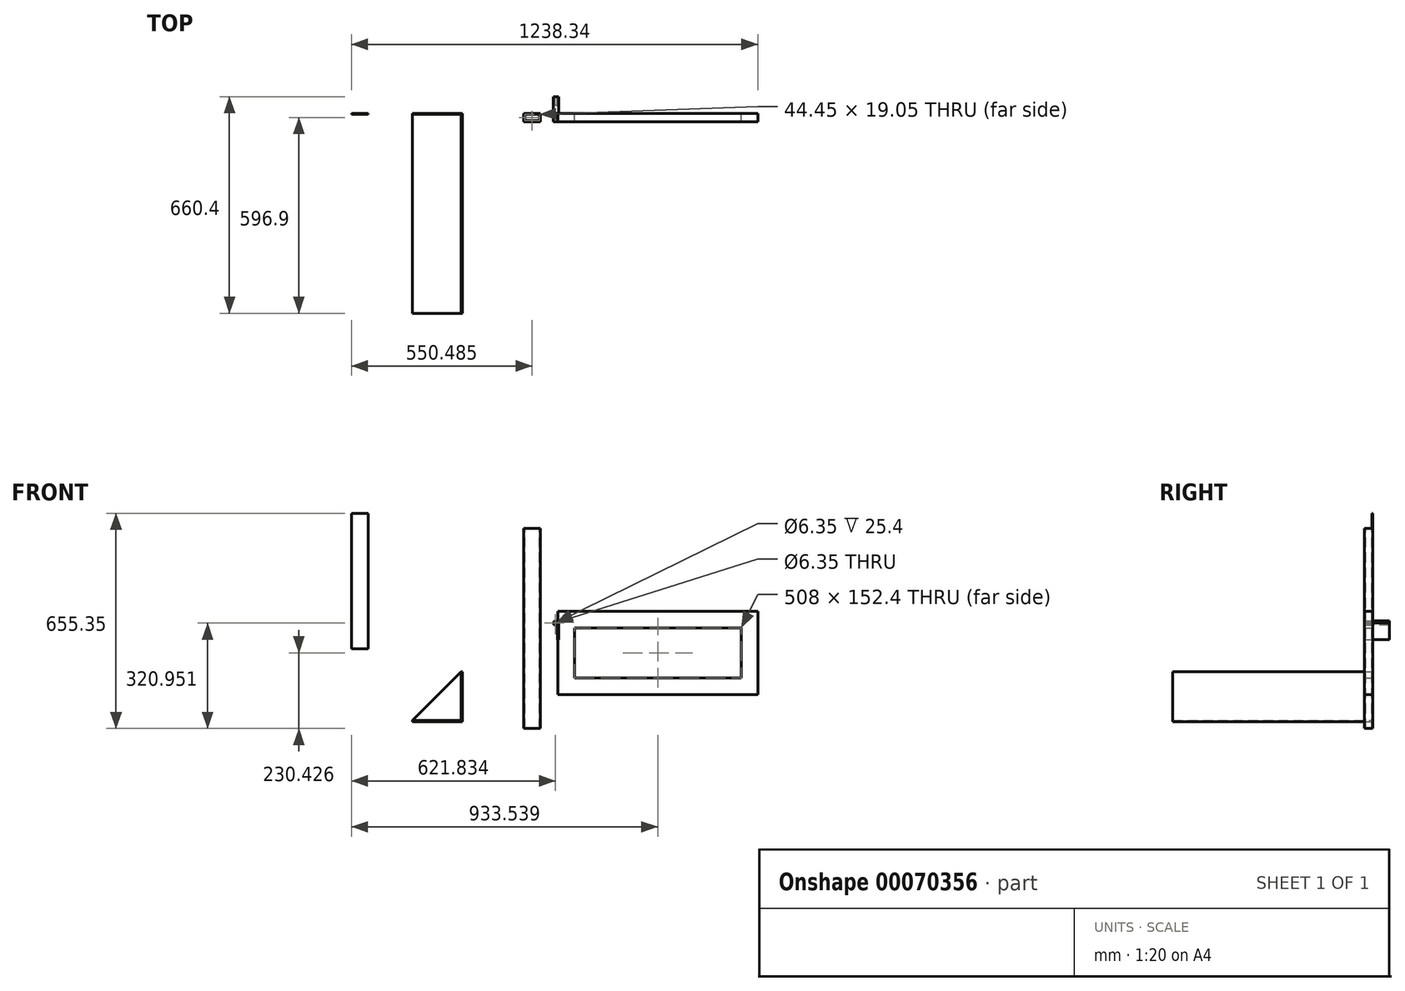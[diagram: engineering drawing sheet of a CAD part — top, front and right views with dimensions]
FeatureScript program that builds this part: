
annotation { "Feature Type Name" : "Feature", "Feature Type Description" : "" }
export const myFeature = defineFeature(function(context is Context, id is Id, definition is map)
    precondition{}
    {
        {
            var Q0;
            Q0=qCreatedBy(makeId("Front.planeOp"),FACE);
            var sketch = newSketch(context, id + "F0", { "sketchPlane" : qUnion([Q0])});
            skLineSegment(sketch, "E0.bottom", {"start": v(-403.8, -283.31) * mm, "end": v(-251.4, -283.31) * mm});
            skLineSegment(sketch, "E0.top", {"start": v(-403.8, -286.49) * mm, "end": v(-251.4, -286.49) * mm});
            skLineSegment(sketch, "E0.left", {"start": v(-403.8, -283.31) * mm, "end": v(-403.8, -286.49) * mm});
            skLineSegment(sketch, "E0.right", {"start": v(-251.4, -283.31) * mm, "end": v(-251.4, -286.49) * mm});
            skLineSegment(sketch, "E1.bottom", {"start": v(-251.4, -286.49) * mm, "end": v(-254.57, -286.49) * mm});
            skLineSegment(sketch, "E1.top", {"start": v(-251.4, -134.09) * mm, "end": v(-254.57, -134.09) * mm});
            skLineSegment(sketch, "E1.left", {"start": v(-251.4, -286.49) * mm, "end": v(-251.4, -134.09) * mm});
            skLineSegment(sketch, "E1.right", {"start": v(-254.57, -286.49) * mm, "end": v(-254.57, -134.09) * mm});
            skLineSegment(sketch, "E2", {"start": v(-254.57, -134.09) * mm, "end": v(-403.8, -283.31) * mm});
            skSolve(sketch);
        }
        {
            var Q0;
            {var subQ4=sQuery(id+"F0.wireOp",EDGE,"E0.top");Q0=makeQuery(id+"F0.imprint","IMPRINT",FACE,{"disambiguationData":[TD([[makeQuery(id+"F0.imprint","IMPRINT",EDGE,{"derivedFrom":subQ4}),1.0]])]});}
            var Q1;
            {var subQ5=sQuery(id+"F0.wireOp",EDGE,"E1.bottom");Q1=makeQuery(id+"F0.imprint","IMPRINT",FACE,{"disambiguationData":[TD([[makeQuery(id+"F0.imprint","IMPRINT",EDGE,{"derivedFrom":subQ5}),-1.0]])]});}
            var Q2;
            {var subQ5=sQuery(id+"F0.wireOp",EDGE,"E1.top");Q2=makeQuery(id+"F0.imprint","IMPRINT",FACE,{"disambiguationData":[TD([[makeQuery(id+"F0.imprint","IMPRINT",EDGE,{"derivedFrom":subQ5}),1.0]])]});}
            extrude(context, id + "F1", {"entities" : qUnion([Q0, Q1, Q2]), "depth" : 609.6 * mm});
        }
        {
            var Q0;
            {var subQ0=sQuery(id+"F0.wireOp",EDGE,"E2");Q0=makeQuery(id+"F0.imprint","IMPRINT",FACE,{"disambiguationData":[TD([[makeQuery(id+"F0.imprint","IMPRINT",EDGE,{"derivedFrom":subQ0}),1.0]])]});}
            extrude(context, id + "F2", {"entities" : qUnion([Q0]), "depth" : 3.17 * mm});
        }
        {
            var Q0;
            Q0=qCreatedBy(makeId("Front.planeOp"),FACE);
            var sketch = newSketch(context, id + "F3", { "sketchPlane" : qUnion([Q0])});
            skCircle(sketch, "E3", {"center": v(32.81, 13.43) * mm, "radius": 6.35 * mm});
            skLineSegment(sketch, "E4.bottom", {"start": v(39.16, 13.43) * mm, "end": v(42.34, 13.43) * mm});
            skLineSegment(sketch, "E4.top", {"start": v(39.16, -37.37) * mm, "end": v(42.34, -37.37) * mm});
            skLineSegment(sketch, "E4.left", {"start": v(39.16, 13.43) * mm, "end": v(39.16, -37.37) * mm});
            skLineSegment(sketch, "E4.right", {"start": v(42.34, 13.43) * mm, "end": v(42.34, -37.37) * mm});
            skCircle(sketch, "E5", {"center": v(32.81, 13.43) * mm, "radius": 3.18 * mm});
            skLineSegment(sketch, "E6", {"start": v(42.34, 13.43) * mm, "end": v(37.05, 18.16) * mm});
            skLineSegment(sketch, "E7", {"start": v(32.81, 7.08) * mm, "end": v(39.16, 7.08) * mm});
            skSolve(sketch);
        }
        {
            var Q0;
            Q0=makeQuery(id+"F3.imprint","IMPRINT",FACE,{"disambiguationData":[TD([[makeQuery(id+"F3.imprint","IMPRINT",EDGE,{"derivedFrom":sQuery(id+"F3.wireOp",EDGE,"E5")}),-1.0]])]});
            var Q1;
            {var subQ0=sQuery(id+"F3.wireOp",EDGE,"E4.bottom");Q1=makeQuery(id+"F3.imprint","IMPRINT",FACE,{"disambiguationData":[TD([[makeQuery(id+"F3.imprint","IMPRINT",EDGE,{"derivedFrom":subQ0}),1.0]])]});}
            var Q2;
            {var subQ3=sQuery(id+"F3.wireOp",EDGE,"E7");Q2=makeQuery(id+"F3.imprint","IMPRINT",FACE,{"disambiguationData":[TD([[makeQuery(id+"F3.imprint","IMPRINT",EDGE,{"derivedFrom":subQ3}),1.0]])]});}
            var Q3;
            {var subQ1=sQuery(id+"F3.wireOp",EDGE,"E4.bottom");Q3=makeQuery(id+"F3.imprint","IMPRINT",FACE,{"disambiguationData":[TD([[makeQuery(id+"F3.imprint","IMPRINT",EDGE,{"derivedFrom":subQ1}),-1.0]])]});}
            extrude(context, id + "F4", {"entities" : qUnion([Q0, Q1, Q2, Q3]), "depth" : 25.4 * mm});
        }
        {
            var Q0;
            {var subQ1=sQuery(id+"F3.wireOp",EDGE,"E4.bottom");Q0=makeQuery(id+"F3.imprint","IMPRINT",FACE,{"disambiguationData":[TD([[makeQuery(id+"F3.imprint","IMPRINT",EDGE,{"derivedFrom":subQ1}),-1.0]])]});}
            var Q1;
            {var subQ3=sQuery(id+"F3.wireOp",EDGE,"E7");Q1=makeQuery(id+"F3.imprint","IMPRINT",FACE,{"disambiguationData":[TD([[makeQuery(id+"F3.imprint","IMPRINT",EDGE,{"derivedFrom":subQ3}),1.0]])]});}
            var Q2;
            {var subQ0=sQuery(id+"F3.wireOp",EDGE,"E4.bottom");Q2=makeQuery(id+"F3.imprint","IMPRINT",FACE,{"disambiguationData":[TD([[makeQuery(id+"F3.imprint","IMPRINT",EDGE,{"derivedFrom":subQ0}),1.0]])]});}
            var Q3;
            Q3=makeQuery(id+"F3.imprint","IMPRINT",FACE,{"disambiguationData":[TD([[makeQuery(id+"F3.imprint","IMPRINT",EDGE,{"derivedFrom":sQuery(id+"F3.wireOp",EDGE,"E5")}),-1.0]])]});
            var Q4;
            Q4=makeQuery(id+"F3.imprint","IMPRINT",FACE,{"disambiguationData":[TD([[makeQuery(id+"F3.imprint","IMPRINT",EDGE,{"derivedFrom":sQuery(id+"F3.wireOp",EDGE,"E5")}),1.0]])]});
            extrude(context, id + "F5", {"entities" : qUnion([Q0, Q1, Q2, Q3, Q4]), "oppositeDirection" : true, "depth" : 25.4 * mm});
        }
        {
            var Q0;
            Q0=makeQuery(id+"F5.opExtrude","CAP_FACE",FACE,{"disambiguationData":[OSD([sQuery(id+"F3.wireOp",EDGE,"E3"),sQuery(id+"F3.wireOp",EDGE,"E4.top"),sQuery(id+"F3.wireOp",EDGE,"E4.left"),sQuery(id+"F3.wireOp",EDGE,"E4.right"),sQuery(id+"F3.wireOp",EDGE,"E6"),sQuery(id+"F3.wireOp",EDGE,"E7")])],"isStart":false});
            var sketch = newSketch(context, id + "F6", { "sketchPlane" : qUnion([Q0])});
            skCircle(sketch, "E8.0", {"center": v(-32.81, 13.43) * mm, "radius": 3.18 * mm});
            skSolve(sketch);
        }
        {
            var Q0;
            Q0=makeQuery(id+"F6.imprint","IMPRINT",FACE,{"disambiguationData":[TD([[makeQuery(id+"F6.imprint","IMPRINT",EDGE,{"derivedFrom":sQuery(id+"F6.wireOp",EDGE,"E8.0")}),-1.0]])]});
            extrude(context, id + "F7", {"entities" : qUnion([Q0]), "operationType" : NewBodyOperationType.ADD, "depth" : 25.4 * mm});
        }
        {
            var Q0;
            Q0=qCreatedBy(makeId("Front.planeOp"),FACE);
            var sketch = newSketch(context, id + "F8", { "sketchPlane" : qUnion([Q0])});
            skLineSegment(sketch, "E9.bottom", {"start": v(-13.13, 302.08) * mm, "end": v(-63.93, 302.08) * mm});
            skLineSegment(sketch, "E9.top", {"start": v(-13.13, -307.52) * mm, "end": v(-63.93, -307.52) * mm});
            skLineSegment(sketch, "E9.left", {"start": v(-13.13, 302.08) * mm, "end": v(-13.13, -307.52) * mm});
            skLineSegment(sketch, "E9.right", {"start": v(-63.93, 302.08) * mm, "end": v(-63.93, -307.52) * mm});
            skSolve(sketch);
        }
        {
            var Q0;
            Q0 = qSketchRegion(id + "F8", true);
            extrude(context, id + "F9", {"entities" : qUnion([Q0]), "depth" : 25.4 * mm});
        }
        {
            var Q0;
            Q0=makeQuery(id+"F9.opExtrude","SWEPT_FACE",FACE,{"disambiguationData":[OSD([sQuery(id+"F8.wireOp",EDGE,"E9.bottom")])]});
            var sketch = newSketch(context, id + "F10", { "sketchPlane" : qUnion([Q0])});
            skLineSegment(sketch, "E10.0", {"start": v(-13.13, -25.4) * mm, "end": v(-63.93, -25.4) * mm});
            skLineSegment(sketch, "E10.1", {"start": v(-13.13, -25.4) * mm, "end": v(-13.13, 0) * mm});
            skLineSegment(sketch, "E10.2", {"start": v(-13.13, 0) * mm, "end": v(-63.93, 0) * mm});
            skLineSegment(sketch, "E10.3", {"start": v(-63.93, -25.4) * mm, "end": v(-63.93, 0) * mm});
            skLineSegment(sketch, "E11.0", {"start": v(-16.3, -22.23) * mm, "end": v(-60.76, -22.23) * mm});
            skLineSegment(sketch, "E11.1", {"start": v(-16.3, -22.23) * mm, "end": v(-16.3, -3.18) * mm});
            skLineSegment(sketch, "E11.2", {"start": v(-16.3, -3.18) * mm, "end": v(-60.76, -3.18) * mm});
            skLineSegment(sketch, "E11.3", {"start": v(-60.76, -22.23) * mm, "end": v(-60.76, -3.18) * mm});
            skSolve(sketch);
        }
        {
            var Q0;
            Q0=makeQuery(id+"F10.imprint","IMPRINT",FACE,{"disambiguationData":[TD([[makeQuery(id+"F10.imprint","IMPRINT",EDGE,{"derivedFrom":sQuery(id+"F10.wireOp",EDGE,"E11.0")}),-1.0]])]});
            extrude(context, id + "F11", {"entities" : qUnion([Q0]), "operationType" : NewBodyOperationType.REMOVE, "endBound" : BoundingType.THROUGH_ALL, "oppositeDirection" : true, "depth" : 25.4 * mm});
        }
        {
            var Q0;
            Q0=qCreatedBy(makeId("Front.planeOp"),FACE);
            var sketch = newSketch(context, id + "F12", { "sketchPlane" : qUnion([Q0])});
            skLineSegment(sketch, "E12.bottom", {"start": v(649.32, 49.9) * mm, "end": v(39.72, 49.9) * mm});
            skLineSegment(sketch, "E12.top", {"start": v(649.32, -204.1) * mm, "end": v(39.72, -204.1) * mm});
            skLineSegment(sketch, "E12.left", {"start": v(649.32, 49.9) * mm, "end": v(649.32, -204.1) * mm});
            skLineSegment(sketch, "E12.right", {"start": v(39.72, 49.9) * mm, "end": v(39.72, -204.1) * mm});
            skLineSegment(sketch, "E13.bottom", {"start": v(598.52, -0.9) * mm, "end": v(90.52, -0.9) * mm});
            skLineSegment(sketch, "E13.top", {"start": v(598.52, -153.3) * mm, "end": v(90.52, -153.3) * mm});
            skLineSegment(sketch, "E13.left", {"start": v(598.52, -0.9) * mm, "end": v(598.52, -153.3) * mm});
            skLineSegment(sketch, "E13.right", {"start": v(90.52, -0.9) * mm, "end": v(90.52, -153.3) * mm});
            skSolve(sketch);
        }
        {
            var Q0;
            Q0=makeQuery(id+"F12.imprint","IMPRINT",FACE,{"disambiguationData":[TD([[makeQuery(id+"F12.imprint","IMPRINT",EDGE,{"derivedFrom":sQuery(id+"F12.wireOp",EDGE,"E12.bottom")}),1.0]])]});
            extrude(context, id + "F13", {"entities" : qUnion([Q0]), "depth" : 25.4 * mm});
        }
        {
            var Q0;
            Q0=qCreatedBy(makeId("Front.planeOp"),FACE);
            var sketch = newSketch(context, id + "F14", { "sketchPlane" : qUnion([Q0])});
            skLineSegment(sketch, "E14.bottom", {"start": v(-538.22, 347.83) * mm, "end": v(-589.02, 347.83) * mm});
            skLineSegment(sketch, "E14.top", {"start": v(-538.22, -64.3) * mm, "end": v(-589.02, -64.3) * mm});
            skLineSegment(sketch, "E14.left", {"start": v(-538.22, 347.83) * mm, "end": v(-538.22, -64.3) * mm});
            skLineSegment(sketch, "E14.right", {"start": v(-589.02, 347.83) * mm, "end": v(-589.02, -64.3) * mm});
            skSolve(sketch);
        }
        {
            var Q0;
            Q0=makeQuery(id+"F14.imprint","IMPRINT",FACE,{"disambiguationData":[TD([[makeQuery(id+"F14.imprint","IMPRINT",EDGE,{"derivedFrom":sQuery(id+"F14.wireOp",EDGE,"E14.bottom")}),1.0]])]});
            extrude(context, id + "F15", {"entities" : qUnion([Q0]), "depth" : 3.17 * mm});
        }
    });
